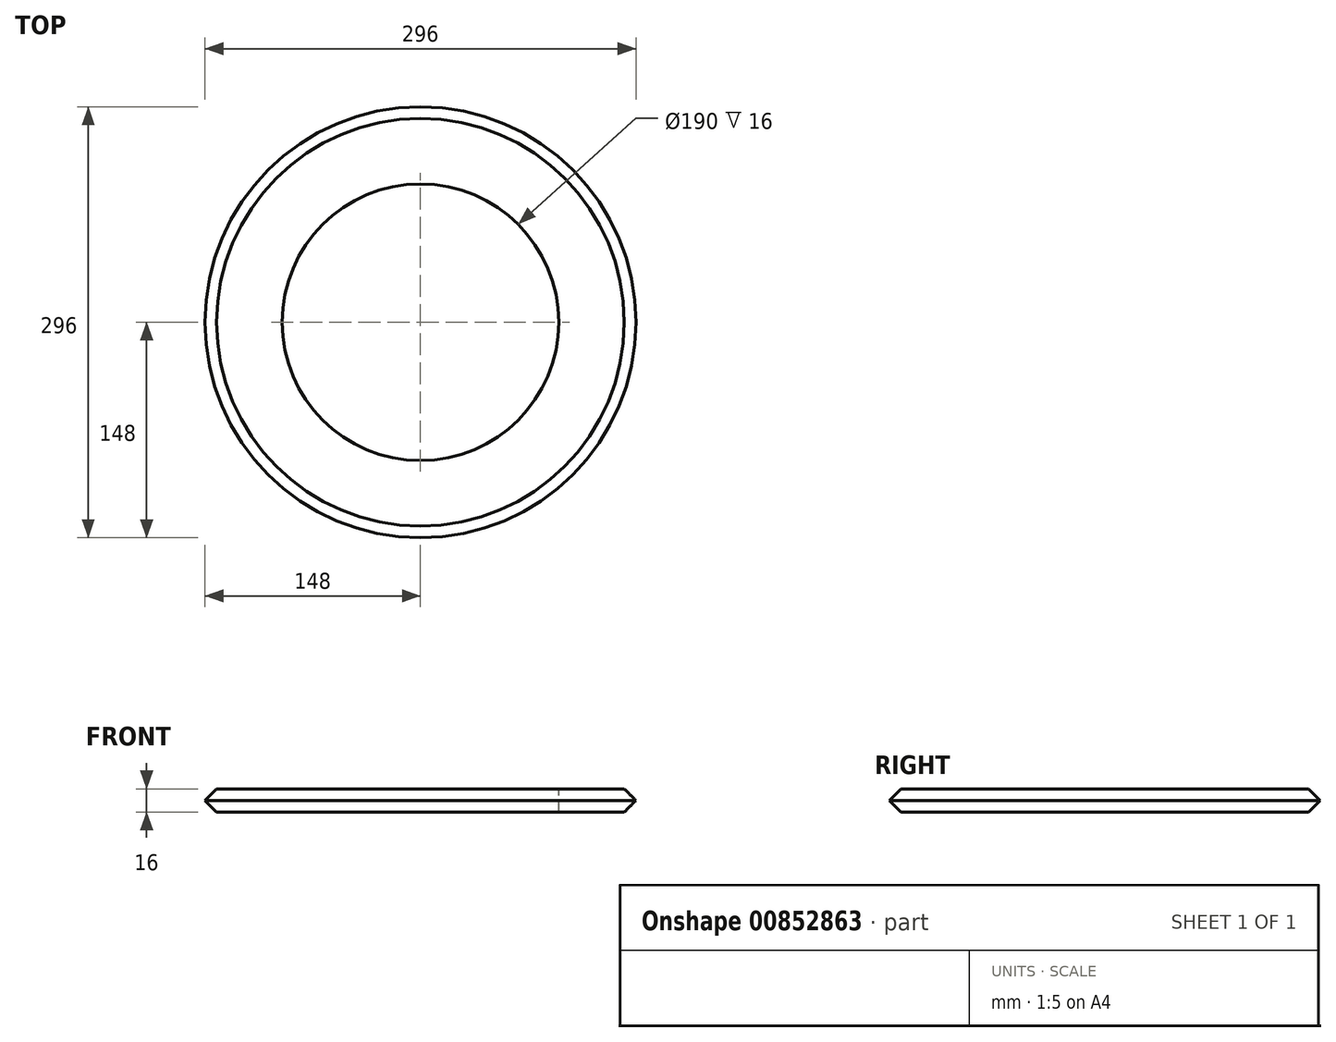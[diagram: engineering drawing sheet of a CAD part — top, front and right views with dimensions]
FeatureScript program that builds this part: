
annotation { "Feature Type Name" : "Feature", "Feature Type Description" : "" }
export const myFeature = defineFeature(function(context is Context, id is Id, definition is map)
    precondition{}
    {
        {
            var Q0;
            Q0=qCreatedBy(makeId("Front.planeOp"),FACE);
            var sketch = newSketch(context, id + "F0", { "sketchPlane" : qUnion([Q0])});
            skLineSegment(sketch, "E0.bottom", {"start": v(95, 0) * mm, "end": v(140, 0) * mm});
            skLineSegment(sketch, "E0.top", {"start": v(95, -16) * mm, "end": v(140, -16) * mm});
            skLineSegment(sketch, "E0.left", {"start": v(95, 0) * mm, "end": v(95, -16) * mm});
            skLineSegment(sketch, "E1", {"start": v(140, -16) * mm, "end": v(148, -8) * mm});
            skLineSegment(sketch, "E2", {"start": v(0, 0) * mm, "end": v(0, -223.71) * mm, "construction": true});
            skLineSegment(sketch, "E3", {"start": v(140, -16) * mm, "end": v(0, -156) * mm, "construction": true});
            skLineSegment(sketch, "E4", {"start": v(148, -8) * mm, "end": v(140, 0) * mm});
            skPoint(sketch, "E5.orphan", {"position": v(156, 0) * mm});
            skSolve(sketch);
        }
        {
            var Q0;
            Q0=makeQuery(id+"F0.imprint","IMPRINT",FACE,{"disambiguationData":[TD([[makeQuery(id+"F0.imprint","IMPRINT",EDGE,{"derivedFrom":sQuery(id+"F0.wireOp",EDGE,"E0.bottom")}),-1.0]])]});
            var Q1;
            Q1=sQuery(id+"F0.wireOp",EDGE,"E2");
            revolve(context, id + "F1", {"surfaceOperationType" : NewSurfaceOperationType.NEW, "entities" : qUnion([Q0]), "axis" : qUnion([Q1]), "revolveType" : RevolveType.FULL});
        }
        {
            var Q0;
            Q0=makeQuery(id+"F1.opRevolve","SWEPT_FACE",FACE,{"disambiguationData":[OSD([sQuery(id+"F0.wireOp",EDGE,"E0.bottom")])]});
            var sketch = newSketch(context, id + "F2", { "sketchPlane" : qUnion([Q0])});
            skLineSegment(sketch, "E6", {"start": v(156, 0) * mm, "end": v(156, -90.98) * mm, "construction": true});
            skLineSegment(sketch, "E7", {"start": v(156, 0) * mm, "end": v(156, 56.3) * mm, "construction": true});
            skSolve(sketch);
        }
        {
            var Q0;
            Q0=sQuery(id+"F2.wireOp",EDGE,"E6");
            cPlane(context, id + "F3", {"entities" : qUnion([Q0]), "cplaneType" : CPlaneType.LINE_ANGLE, "offset" : 25 * mm, "angle" : 45 * degree, "width" : 150 * mm, "height" : 150 * mm});
        }
    });
